# Revit family: P200921MX-077c_MVW8230HC
name_source: partatom
category: Specialty Equipment
units: mm (PartAtom-declared; Revit-internal decimal feet)

## family parameters
Always vertical = No
Cut with Voids When Loaded = No
Enable Cutting in Views = No
Maintain Annotation Orientation = No
Part Type = Normal
Room Calculation Point = No
Round Connector Dimension = Use Diameter
Shared = No
Work Plane-Based = No

## types (1)
- MVW8230HC
    Accent Material = ARCAT - Plastic - Gray
    Amps = 0 A
    Back Panel Material = ARCAT - Metal - Aluminum
    Body Material = ARCAT - Metal - Steel - Gray
    Clearance Material = ARCAT - Clearance
    Default Elevation = 0"
    Depth = 27 7/8"
    Description = Smart Capable Top Load Washer with Extra Power Button - 5.2 cu. ft.
Laveuse intelligente à chargement vertical, Extra Power, 5,2 pi³
    Dimension Guide = https://www.whirlpool.com
    Display Panel Material = ARCAT - Glass - Tempered - Dark Black
    Door Material = ARCAT - Metal - Steel - Stainless
    Energy Guide = https://whirlpool.com
    Family Name = Laundry
    Feature 1 = Most Powerful Cleaning in its class driven by the Heavy Duty cycle with Extra Power button
Le nettoyage le plus puissant dans sa catégorie, optimisé par le programme intensif et la fonction Extra Power
    Feature 2 = Extra Power button
Extra Power button
    Feature 3 = Smart capable appliance
Électroménager intelligent
    Glass Material = ARCAT - Glass - Tempered - Black
    Handle Material = ARCAT - Metal - Steel - Stainless
    Height = 42 7/8"
    Knob Material = ARCAT - Metal - Steel - Stainless
    Leg Material = ARCAT - Plastic - White
    Manufacturer = Maytag
    Model = MVW8230HC
    Voltage = 0 V
    Width = 27 1/4"

## geometry (parser evidence)
native form markers: Sweep x7
no freeform markers — native parametric forms only
